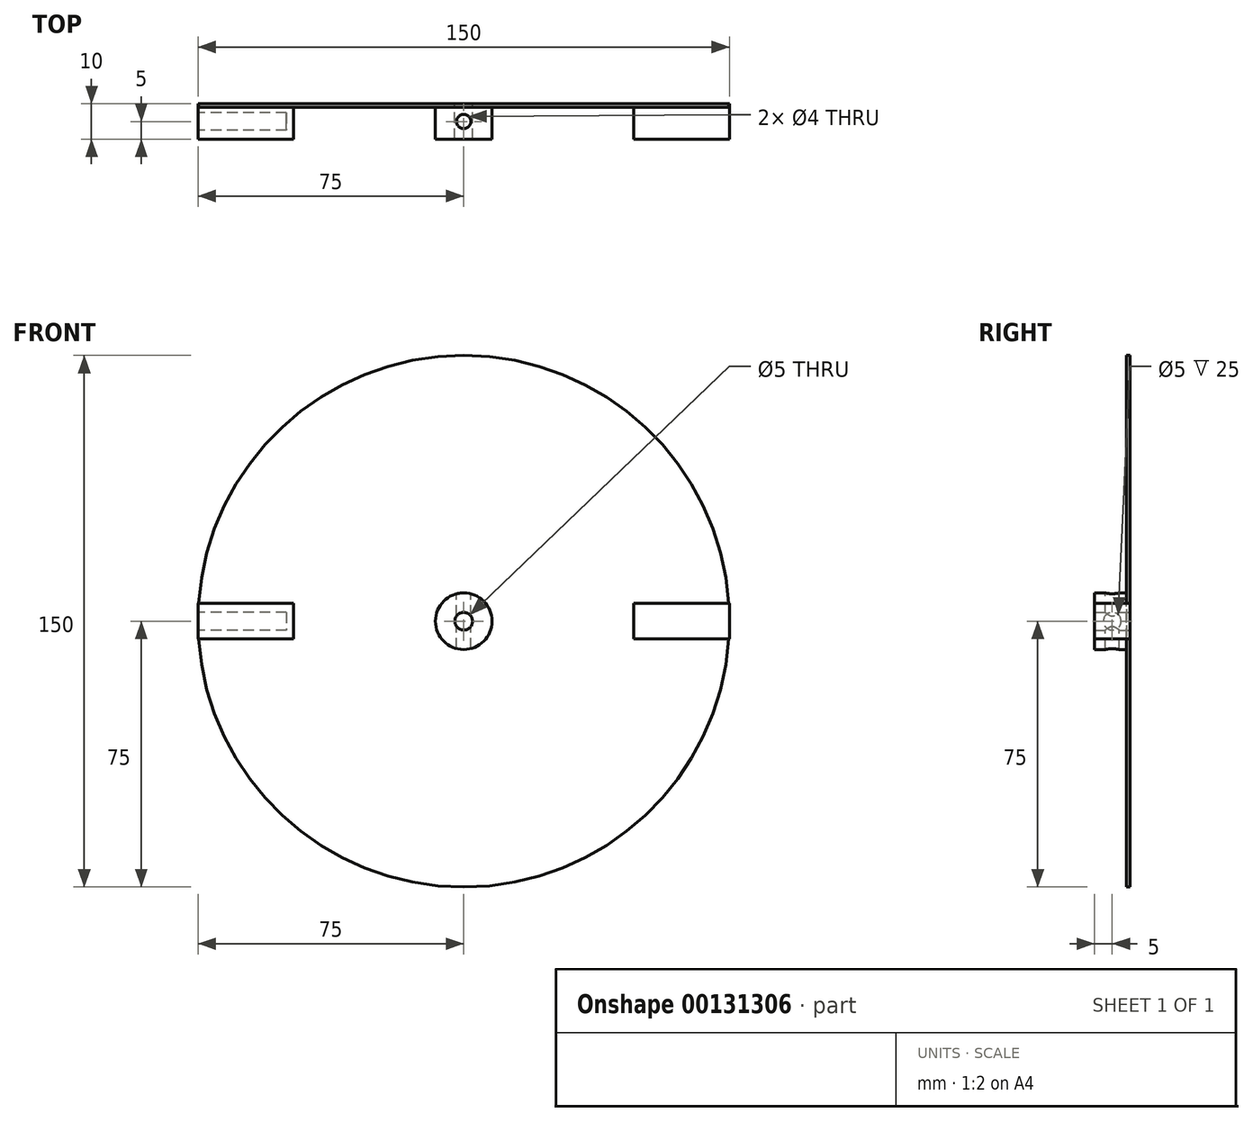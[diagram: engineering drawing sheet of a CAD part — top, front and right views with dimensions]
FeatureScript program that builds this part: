
annotation { "Feature Type Name" : "Feature", "Feature Type Description" : "" }
export const myFeature = defineFeature(function(context is Context, id is Id, definition is map)
    precondition{}
    {
        {
            var Q0;
            Q0=qCreatedBy(makeId("Front.planeOp"),FACE);
            var sketch = newSketch(context, id + "F0", { "sketchPlane" : qUnion([Q0])});
            skCircle(sketch, "E0", {"center": v(0, 0) * mm, "radius": 2.5 * mm});
            skLineSegment(sketch, "E1.bottom", {"start": v(6.24, 5) * mm, "end": v(48, 5) * mm, "construction": true});
            skLineSegment(sketch, "E1.top", {"start": v(6.24, -5) * mm, "end": v(48, -5) * mm, "construction": true});
            skLineSegment(sketch, "E1.left", {"start": v(6.24, 5) * mm, "end": v(6.24, -5) * mm, "construction": true});
            skLineSegment(sketch, "E1.right", {"start": v(75, 5) * mm, "end": v(75, -5) * mm});
            skLineSegment(sketch, "E2.bottom", {"start": v(-6.24, 5) * mm, "end": v(-48, 5) * mm, "construction": true});
            skLineSegment(sketch, "E2.top", {"start": v(-6.24, -5) * mm, "end": v(-48, -5) * mm, "construction": true});
            skLineSegment(sketch, "E2.left", {"start": v(-6.24, 5) * mm, "end": v(-6.24, -5) * mm, "construction": true});
            skLineSegment(sketch, "E2.right", {"start": v(-75, 5) * mm, "end": v(-75, -5) * mm});
            skLineSegment(sketch, "E3", {"start": v(-6.24, 5) * mm, "end": v(6.24, 5) * mm, "construction": true});
            skLineSegment(sketch, "E4", {"start": v(-6.24, -5) * mm, "end": v(6.24, -5) * mm, "construction": true});
            skArc(sketch, "E5", {"start": v(-6.24, 5) * mm, "mid": v(-8, 0) * mm, "end": v(-6.24, -5) * mm});
            skArc(sketch, "E6", {"start": v(-6.24, -5) * mm, "mid": v(0, -8) * mm, "end": v(6.24, -5) * mm});
            skArc(sketch, "E7", {"start": v(6.24, -5) * mm, "mid": v(8, 0) * mm, "end": v(6.24, 5) * mm});
            skArc(sketch, "E8", {"start": v(6.24, 5) * mm, "mid": v(0, 8) * mm, "end": v(-6.24, 5) * mm});
            skLineSegment(sketch, "E9", {"start": v(-48, 5) * mm, "end": v(-48, -5) * mm});
            skLineSegment(sketch, "E10", {"start": v(48, 5) * mm, "end": v(48, -5) * mm});
            skLineSegment(sketch, "E11", {"start": v(-48, 5) * mm, "end": v(-75, 5) * mm});
            skLineSegment(sketch, "E12", {"start": v(-48, -5) * mm, "end": v(-75, -5) * mm});
            skLineSegment(sketch, "E13", {"start": v(48, -5) * mm, "end": v(75, -5) * mm});
            skLineSegment(sketch, "E14", {"start": v(48, 5) * mm, "end": v(75, 5) * mm});
            skSolve(sketch);
        }
        {
            var Q0;
            Q0=qSketchRegion(id+"F0",true);
            extrude(context, id + "F1", {"entities" : qUnion([Q0]), "depth" : 10 * mm});
        }
        {
            var Q0;
            Q0=makeQuery(id+"F1.opExtrude","CAP_FACE",FACE,{"disambiguationData":[OSD([sQuery(id+"F0.wireOp",EDGE,"E0"),sQuery(id+"F0.wireOp",EDGE,"E5"),sQuery(id+"F0.wireOp",EDGE,"E6"),sQuery(id+"F0.wireOp",EDGE,"E7"),sQuery(id+"F0.wireOp",EDGE,"E8")])],"isStart":true});
            var sketch = newSketch(context, id + "F2", { "sketchPlane" : qUnion([Q0])});
            skCircle(sketch, "E15", {"center": v(0, 0) * mm, "radius": 75 * mm});
            skCircle(sketch, "E16.0", {"center": v(0, 0) * mm, "radius": 2.5 * mm});
            skSolve(sketch);
        }
        {
            var Q0;
            Q0 = qSketchRegion(id + "F2", true);
            extrude(context, id + "F3", {"entities" : qUnion([Q0]), "operationType" : NewBodyOperationType.ADD, "oppositeDirection" : true, "depth" : 1 * mm});
        }
        {
            var Q0;
            Q0=makeQuery(id+"F1.opExtrude","SWEPT_FACE",FACE,{"disambiguationData":[OSD([sQuery(id+"F0.wireOp",EDGE,"E2.right")])]});
            var sketch = newSketch(context, id + "F4", { "sketchPlane" : qUnion([Q0])});
            skCircle(sketch, "E17", {"center": v(5, 0) * mm, "radius": 2.5 * mm});
            skLineSegment(sketch, "E18", {"start": v(0, 5) * mm, "end": v(10, -5) * mm, "construction": true});
            skSolve(sketch);
        }
        {
            var Q0;
            Q0=qSketchRegion(id+"F4",true);
            extrude(context, id + "F5", {"entities" : qUnion([Q0]), "operationType" : NewBodyOperationType.REMOVE, "oppositeDirection" : true, "depth" : 25 * mm});
        }
        {
            var Q0;
            Q0=qCreatedBy(makeId("Top.planeOp"),FACE);
            var sketch = newSketch(context, id + "F6", { "sketchPlane" : qUnion([Q0])});
            skCircle(sketch, "E19", {"center": v(0, -5) * mm, "radius": 2 * mm});
            skSolve(sketch);
        }
        {
            var Q0;
            Q0=qSketchRegion(id+"F6",true);
            extrude(context, id + "F7", {"entities" : qUnion([Q0]), "operationType" : NewBodyOperationType.REMOVE, "endBound" : BoundingType.THROUGH_ALL, "oppositeDirection" : true, "depth" : 25 * mm, "hasSecondDirection" : true, "secondDirectionBound" : SecondDirectionBoundingType.THROUGH_ALL, "secondDirectionOppositeDirection" : false, "secondDirectionDepth" : 25 * mm});
        }
    });
